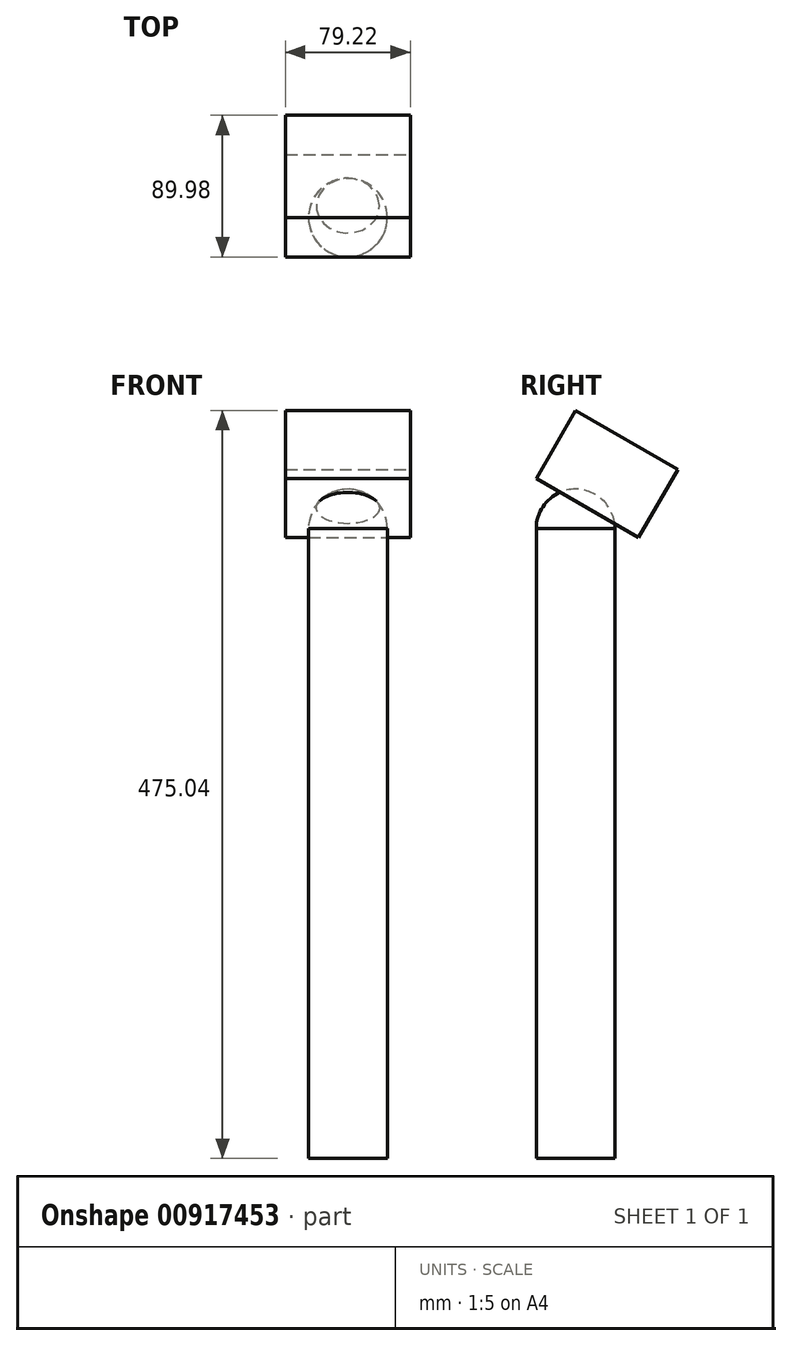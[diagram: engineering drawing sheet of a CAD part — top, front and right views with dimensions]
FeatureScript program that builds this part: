
annotation { "Feature Type Name" : "Feature", "Feature Type Description" : "" }
export const myFeature = defineFeature(function(context is Context, id is Id, definition is map)
    precondition{}
    {
        {
            var Q0;
            Q0=qCreatedBy(makeId("Top.planeOp"),FACE);
            var sketch = newSketch(context, id + "F0", { "sketchPlane" : qUnion([Q0])});
            skCircle(sketch, "E0", {"center": v(0, 0) * mm, "radius": 25 * mm});
            skSolve(sketch);
        }
        {
            var Q0;
            Q0=makeQuery(id+"F0.imprint","IMPRINT",FACE,{"disambiguationData":[TD([[makeQuery(id+"F0.imprint","IMPRINT",EDGE,{"derivedFrom":sQuery(id+"F0.wireOp",EDGE,"E0")}),1.0]])]});
            extrude(context, id + "F1", {"entities" : qUnion([Q0]), "depth" : 400 * mm, "offsetDistance" : 25 * mm});
        }
        {
            var Q0;
            Q0=makeQuery(id+"F1.opExtrude","CAP_FACE",FACE,{"disambiguationData":[OSD([sQuery(id+"F0.wireOp",EDGE,"E0")])],"isStart":false});
            var sketch = newSketch(context, id + "F2", { "sketchPlane" : qUnion([Q0])});
            skLineSegment(sketch, "E1", {"start": v(25, 0) * mm, "end": v(-25, 0) * mm});
            skArc(sketch, "E2", {"start": v(25, 0) * mm, "mid": v(0, 24.98) * mm, "end": v(-25, 0) * mm});
            skSolve(sketch);
        }
        {
            var Q0;
            {var subQ0=sQuery(id+"F2.wireOp",EDGE,"E1");Q0=makeQuery(id+"F2.imprint","IMPRINT",FACE,{"disambiguationData":[TD([[makeQuery(id+"F2.imprint","IMPRINT",EDGE,{"derivedFrom":subQ0}),1.0]])]});}
            var Q1;
            Q1=sQuery(id+"F2.wireOp",EDGE,"E2");
            var Q2;
            Q2=sQuery(id+"F2.wireOp",EDGE,"E1");
            revolve(context, id + "F3", {"surfaceOperationType" : NewSurfaceOperationType.NEW, "entities" : qUnion([Q0]), "surfaceEntities" : qUnion([Q1]), "axis" : qUnion([Q2]), "revolveType" : RevolveType.ONE_DIRECTION, "angle" : 180 * degree});
        }
        {
            var Q0;
            Q0=qCreatedBy(makeId("Top.planeOp"),FACE);
            cPlane(context, id + "F4", {"entities" : qUnion([Q0]), "cplaneType" : CPlaneType.OFFSET, "offset" : 600 * mm, "width" : 150 * mm, "height" : 150 * mm});
        }
        {
            var Q0;
            Q0=qCreatedBy(id+"F4.planeOp",FACE);
            var sketch = newSketch(context, id + "F5", { "sketchPlane" : qUnion([Q0])});
            skLineSegment(sketch, "E3.bottom", {"start": v(-39.61, 37.5) * mm, "end": v(39.61, 37.5) * mm});
            skLineSegment(sketch, "E3.top", {"start": v(-39.61, -37.5) * mm, "end": v(39.61, -37.5) * mm});
            skLineSegment(sketch, "E3.left", {"start": v(-39.61, 37.5) * mm, "end": v(-39.61, -37.5) * mm});
            skLineSegment(sketch, "E3.right", {"start": v(39.61, 37.5) * mm, "end": v(39.61, -37.5) * mm});
            skPoint(sketch, "E3.middle", {"position": v(0, 0) * mm});
            skSolve(sketch);
        }
        {
            var Q0;
            Q0=makeQuery(id+"F5.imprint","IMPRINT",FACE,{"disambiguationData":[TD([[makeQuery(id+"F5.imprint","IMPRINT",EDGE,{"derivedFrom":sQuery(id+"F5.wireOp",EDGE,"E3.bottom")}),-1.0]])]});
            extrude(context, id + "F6", {"entities" : qUnion([Q0]), "depth" : 50 * mm, "offsetDistance" : 25 * mm});
        }
        {
            var Q0;
            Q0=qCreatedBy(makeId("Front.planeOp"),FACE);
            var sketch = newSketch(context, id + "F7", { "sketchPlane" : qUnion([Q0])});
            skLineSegment(sketch, "E4", {"start": v(0, 762.58) * mm, "end": v(0, -82.67) * mm, "construction": true});
            skSolve(sketch);
        }
        {
            var Q0;
            Q0=makeQuery(id+"F6.opExtrude","SWEPT_BODY",BODY,{"disambiguationData":[OSD([sQuery(id+"F5.wireOp",EDGE,"E3.bottom"),sQuery(id+"F5.wireOp",EDGE,"E3.top"),sQuery(id+"F5.wireOp",EDGE,"E3.left"),sQuery(id+"F5.wireOp",EDGE,"E3.right")])]});
            var Q1;
            Q1=sQuery(id+"F7.wireOp",EDGE,"E4");
            transform(context, id + "F8", {"entities" : qUnion([Q0]), "transformType" : TransformType.TRANSLATION_DISTANCE, "transformDirection" : qUnion([Q1]), "distance" : 185 * mm, "makeCopy" : false});
        }
        {
            var Q0;
            Q0=makeQuery(id+"F3.opRevolve","SWEPT_BODY",BODY,{"disambiguationData":[OSD([sQuery(id+"F0.wireOp",EDGE,"E0"),sQuery(id+"F2.wireOp",EDGE,"E1")])]});
            var Q1;
            Q1=makeQuery(id+"F6.opExtrude","SWEPT_BODY",BODY,{"disambiguationData":[OSD([sQuery(id+"F5.wireOp",EDGE,"E3.bottom"),sQuery(id+"F5.wireOp",EDGE,"E3.top"),sQuery(id+"F5.wireOp",EDGE,"E3.left"),sQuery(id+"F5.wireOp",EDGE,"E3.right")])]});
            booleanBodies(context, id + "F9", {"operationType" : BooleanOperationType.SUBTRACTION, "tools" : qUnion([Q0]), "targets" : qUnion([Q1]), "keepTools" : true});
        }
        {
            var Q0;
            Q0=qCreatedBy(makeId("Front.planeOp"),FACE);
            var sketch = newSketch(context, id + "F10", { "sketchPlane" : qUnion([Q0])});
            skLineSegment(sketch, "E5", {"start": v(72.08, 400) * mm, "end": v(-65.2, 400) * mm, "construction": true});
            skSolve(sketch);
        }
        {
            var Q0;
            Q0=makeQuery(id+"F6.opExtrude","SWEPT_BODY",BODY,{"disambiguationData":[OSD([sQuery(id+"F5.wireOp",EDGE,"E3.bottom"),sQuery(id+"F5.wireOp",EDGE,"E3.top"),sQuery(id+"F5.wireOp",EDGE,"E3.left"),sQuery(id+"F5.wireOp",EDGE,"E3.right")])]});
            var Q1;
            Q1=sQuery(id+"F10.wireOp",EDGE,"E5");
            transform(context, id + "F11", {"entities" : qUnion([Q0]), "transformType" : TransformType.ROTATION, "transformAxis" : qUnion([Q1]), "angle" : 30 * degree, "makeCopy" : false});
        }
    });
